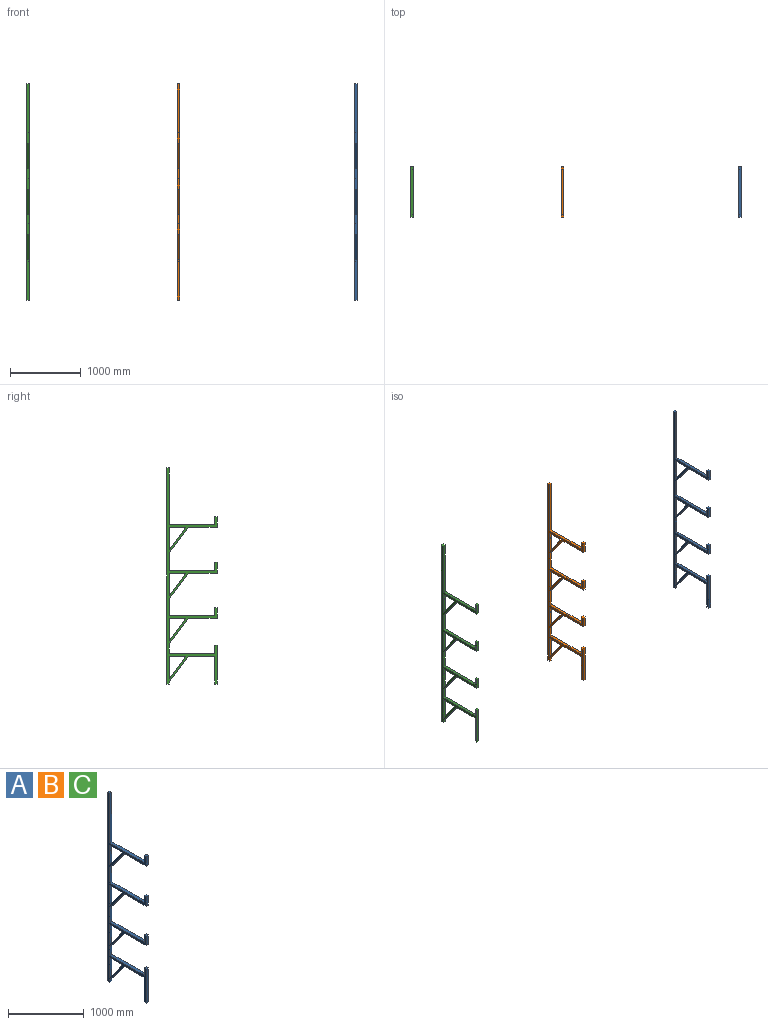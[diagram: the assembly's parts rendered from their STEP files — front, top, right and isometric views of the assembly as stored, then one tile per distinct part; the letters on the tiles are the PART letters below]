
ASSEMBLY  parts=3 mates=3
PART A: 50 faces, bbox 38.1x711.2x3048 mm
  f0: plane 38.1x38.1mm, normal (0,-1,0), area 1451.6mm2, adj f14,f16,f17,f47
  f1: plane 228.6x38.1mm, normal (0,0,-1), area 8709.7mm2, adj f8,f16,f17,f46
  f2: plane 139.7x38.1mm, normal (0,-1,0), area 5322.6mm2, adj f16,f17,f28,f45
  f3: plane 228.6x38.1mm, normal (0,0,-1), area 8709.7mm2, adj f9,f16,f17,f44
  f4: plane 241.3x38.1mm, normal (0,-1,0), area 9193.5mm2, adj f16,f17,f25,f43
  f5: plane 228.6x38.1mm, normal (0,0,-1), area 8709.7mm2, adj f10,f16,f17,f42
  f6: plane 254x38.1mm, normal (0,-1,0), area 9677.4mm2, adj f16,f17,f22,f41
  f7: plane 228.6x38.1mm, normal (0,0,-1), area 8709.7mm2, adj f11,f16,f17,f40
  f8: plane 317.5x38.1mm, normal (0,-1,0), area 12096.7mm2, adj f1,f16,f17,f46
  f9: plane 317.5x38.1mm, normal (0,-1,0), area 12016.9mm2, adj f3,f16,f17,f44,f49
  f10: plane 317.5x38.1mm, normal (0,-1,0), area 12096.8mm2, adj f5,f16,f17,f42
  f11: plane 317.5x38.1mm, normal (0,-1,0), area 12016.9mm2, adj f7,f16,f17,f40,f48
  f12: plane 38.1x38.1mm, normal (0,0,1), area 1451.6mm2, adj f13,f15,f16,f17
  f13: plane 800.1x38.1mm, normal (0,-1,0), area 30483.8mm2, adj f12,f16,f17,f19
  f14: plane 38.1x38.1mm, normal (0,0,-1), area 1451.6mm2, adj f0,f15,f16,f17
  f15: plane 3048x38.1mm, normal (0,1,0), area 115969.1mm2, adj f12,f14,f16,f17,f48,f49
  f16: plane 3048x711.2mm, normal (1,0,0), area 295644.6mm2, adj f0,f1,f2,f3,f4,f5,f6,f7
  f17: plane 3048x711.2mm, normal (-1,0,0), area 295644.6mm2, adj f0,f1,f2,f3,f4,f5,f6,f7
  f18: plane 406.4x38.1mm, normal (0,0,-1), area 15483.8mm2, adj f16,f17,f20,f41
  f19: plane 635x38.1mm, normal (0,0,1), area 24193.5mm2, adj f13,f16,f17,f30
  f20: plane 152.4x38.1mm, normal (0,-1,0), area 5806.4mm2, adj f16,f17,f18,f31
  f21: plane 406.4x38.1mm, normal (0,0,-1), area 15483.8mm2, adj f16,f17,f23,f43
  f22: plane 635x38.1mm, normal (0,0,1), area 24193.5mm2, adj f6,f16,f17,f32
  f23: plane 152.4x38.1mm, normal (0,-1,0), area 5806.4mm2, adj f16,f17,f21,f33
  f24: plane 406.4x38.1mm, normal (0,0,-1), area 15483.8mm2, adj f16,f17,f26,f45
  f25: plane 635x38.1mm, normal (0,0,1), area 24193.5mm2, adj f4,f16,f17,f34
  f26: plane 152.4x38.1mm, normal (0,-1,0), area 5806.4mm2, adj f16,f17,f24,f35
  f27: plane 368.3x38.1mm, normal (0,0,-1), area 14032.2mm2, adj f16,f17,f39,f47
  f28: plane 635x38.1mm, normal (0,0,1), area 24193.5mm2, adj f2,f16,f17,f36
  f29: plane 546.1x38.1mm, normal (0,-1,0), area 20806.4mm2, adj f16,f17,f37,f38
  f30: plane 114.3x38.1mm, normal (0,1,0), area 4354.8mm2, adj f16,f17,f19,f31
  f31: plane 38.1x38.1mm, normal (0,0,1), area 1451.6mm2, adj f16,f17,f20,f30
  f32: plane 114.3x38.1mm, normal (0,1,0), area 4354.8mm2, adj f16,f17,f22,f33
  f33: plane 38.1x38.1mm, normal (0,0,1), area 1451.6mm2, adj f16,f17,f23,f32
  f34: plane 114.3x38.1mm, normal (0,1,0), area 4354.8mm2, adj f16,f17,f25,f35
  f35: plane 38.1x38.1mm, normal (0,0,1), area 1451.6mm2, adj f16,f17,f26,f34
  f36: plane 114.3x38.1mm, normal (0,1,0), area 4354.8mm2, adj f16,f17,f28,f37
  f37: plane 38.1x38.1mm, normal (0,0,1), area 1451.6mm2, adj f16,f17,f29,f36
  f38: plane 38.1x38.1mm, normal (0,0,-1), area 1451.6mm2, adj f16,f17,f29,f39
  f39: plane 393.7x38.1mm, normal (0,1,0), area 15000mm2, adj f16,f17,f27,f38
  f40: plane 317.5x228.6mm, normal (0,0.81,0.58), area 14906mm2, adj f7,f11,f16,f17
  f41: plane 355.6x266.7mm, normal (0,-0.8,-0.6), area 16935.5mm2, adj f6,f16,f17,f18
  f42: plane 317.5x228.6mm, normal (0,0.81,0.58), area 14906mm2, adj f5,f10,f16,f17
  f43: plane 355.6x266.7mm, normal (0,-0.8,-0.6), area 16935.5mm2, adj f4,f16,f17,f21
  f44: plane 317.5x228.6mm, normal (0,0.81,0.58), area 14906mm2, adj f3,f9,f16,f17
  f45: plane 355.6x266.7mm, normal (0,-0.8,-0.6), area 16935.5mm2, adj f2,f16,f17,f24
  f46: plane 317.5x228.6mm, normal (0,0.81,0.58), area 14906mm2, adj f1,f8,f16,f17
  f47: plane 355.6x266.7mm, normal (0,-0.8,-0.6), area 16935.5mm2, adj f0,f16,f17,f27
  f48: cylinder r=5.04mm len=38.1mm, axis (0,-1,0), area 1207mm2, adj f11,f15
  f49: cylinder r=5.04mm len=38.1mm, axis (0,-1,0), area 1207mm2, adj f9,f15
PART B: same geometry as A
PART C: same geometry as A
PLACE A t=(-6411.06,624.84,-251.3)mm
PLACE B t=(-8912.96,624.84,-251.3)mm
PLACE C t=(-11033.86,624.84,-251.3)mm
MATE parallel A.f16 <-> B.f17  axis (1,0,0) through (-6372.96,633.8,2710.16)mm
MATE parallel B.f16 <-> C.f17  axis (1,0,0) through (-8874.86,633.8,2710.16)mm
MATE parallel A.f16 <-> C.f17  axis (1,0,0) through (-6372.96,633.8,2710.16)mm
